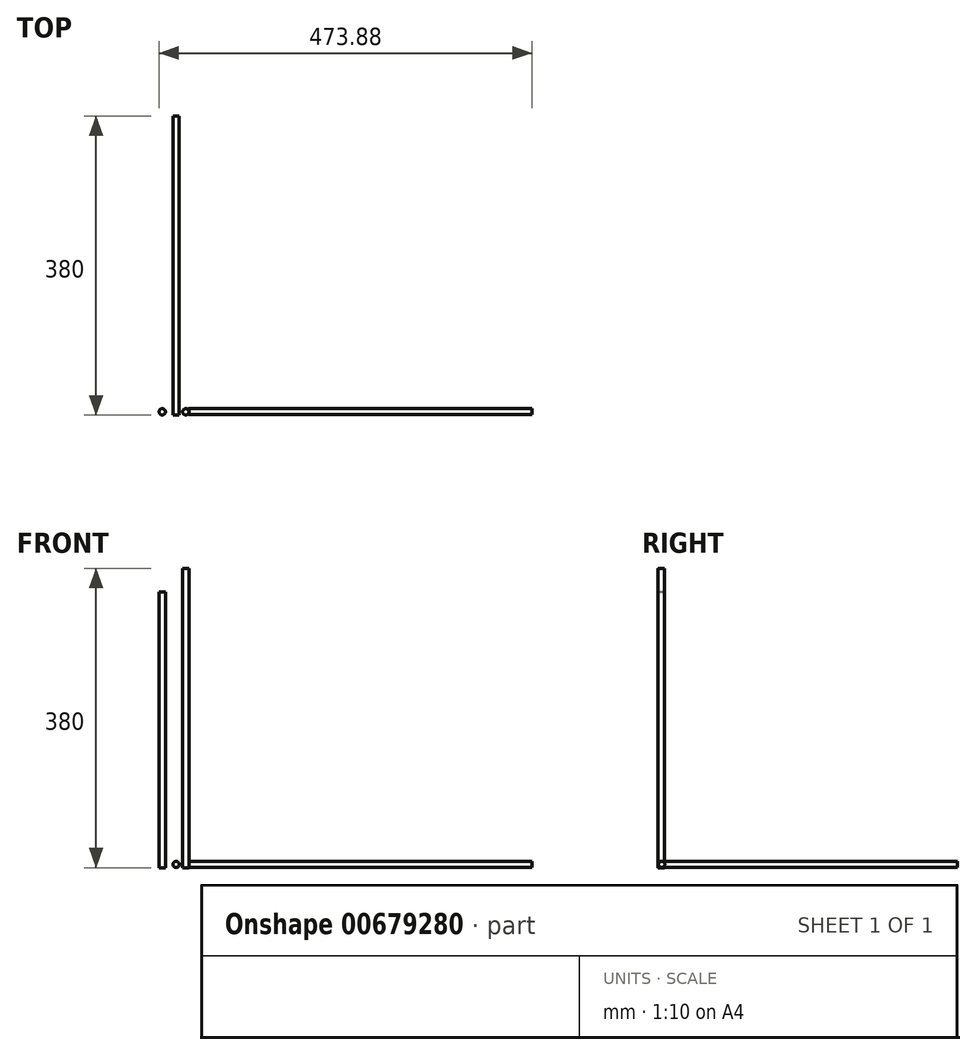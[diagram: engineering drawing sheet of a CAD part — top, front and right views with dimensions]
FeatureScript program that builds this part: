
annotation { "Feature Type Name" : "Feature", "Feature Type Description" : "" }
export const myFeature = defineFeature(function(context is Context, id is Id, definition is map)
    precondition{}
    {
        {
            var Q0;
            Q0=qCreatedBy(makeId("Top.planeOp"),FACE);
            var sketch = newSketch(context, id + "F0", { "sketchPlane" : qUnion([Q0])});
            skCircle(sketch, "E0", {"center": v(-4, 4.03) * mm, "radius": 4 * mm});
            skCircle(sketch, "E1", {"center": v(-33.88, 4.03) * mm, "radius": 4 * mm});
            skSolve(sketch);
        }
        {
            var Q0;
            Q0=makeQuery(id+"F0.imprint","IMPRINT",FACE,{"disambiguationData":[TD([[makeQuery(id+"F0.imprint","IMPRINT",EDGE,{"derivedFrom":sQuery(id+"F0.wireOp",EDGE,"E0")}),1.0]])]});
            extrude(context, id + "F1", {"entities" : qUnion([Q0]), "depth" : 380 * mm, "offsetDistance" : 25 * mm});
        }
        {
            var Q0;
            Q0=qCreatedBy(makeId("Front.planeOp"),FACE);
            var sketch = newSketch(context, id + "F2", { "sketchPlane" : qUnion([Q0])});
            skCircle(sketch, "E2", {"center": v(-16.24, 4.03) * mm, "radius": 4 * mm});
            skSolve(sketch);
        }
        {
            var Q0;
            Q0=qSketchRegion(id+"F2",true);
            extrude(context, id + "F3", {"entities" : qUnion([Q0]), "oppositeDirection" : true, "depth" : 380 * mm, "offsetDistance" : 25 * mm});
        }
        {
            var Q0;
            Q0=qCreatedBy(makeId("Right.planeOp"),FACE);
            var sketch = newSketch(context, id + "F4", { "sketchPlane" : qUnion([Q0])});
            skCircle(sketch, "E3", {"center": v(4.57, 4.13) * mm, "radius": 4 * mm});
            skSolve(sketch);
        }
        {
            var Q0;
            Q0=qSketchRegion(id+"F4",true);
            extrude(context, id + "F5", {"entities" : qUnion([Q0]), "depth" : 436 * mm, "offsetDistance" : 25 * mm});
        }
        {
            var Q0;
            Q0=makeQuery(id+"F0.imprint","IMPRINT",FACE,{"disambiguationData":[TD([[makeQuery(id+"F0.imprint","IMPRINT",EDGE,{"derivedFrom":sQuery(id+"F0.wireOp",EDGE,"E1")}),1.0]])]});
            extrude(context, id + "F6", {"entities" : qUnion([Q0]), "depth" : 350 * mm, "offsetDistance" : 25 * mm});
        }
    });
